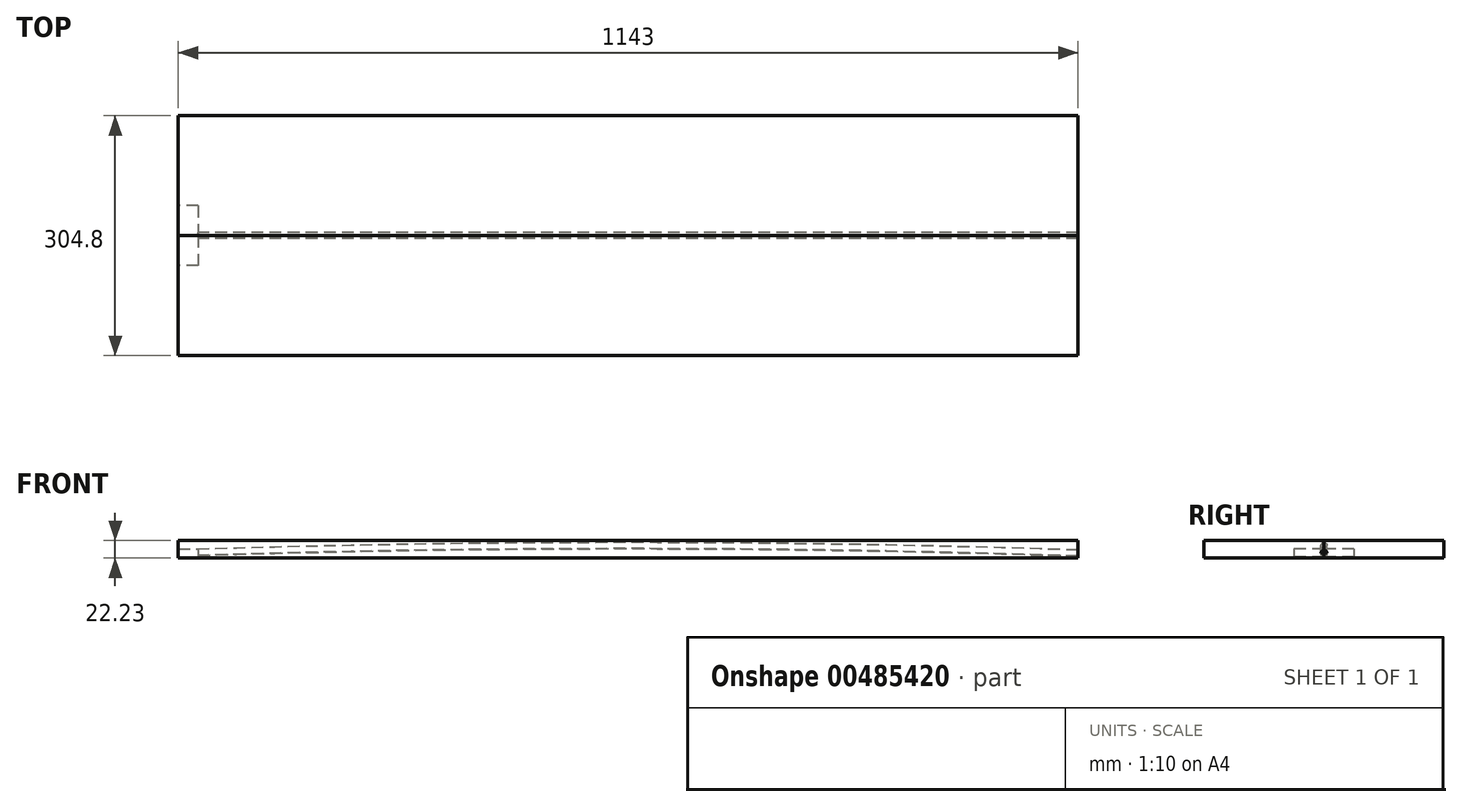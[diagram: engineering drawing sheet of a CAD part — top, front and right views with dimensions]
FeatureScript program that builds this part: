
annotation { "Feature Type Name" : "Feature", "Feature Type Description" : "" }
export const myFeature = defineFeature(function(context is Context, id is Id, definition is map)
    precondition{}
    {
        {
            var Q0;
            Q0=qCreatedBy(makeId("Front.planeOp"),FACE);
            var sketch = newSketch(context, id + "F0", { "sketchPlane" : qUnion([Q0])});
            skLineSegment(sketch, "E0.bottom", {"start": v(0, -22.23) * mm, "end": v(-1143, -22.23) * mm});
            skLineSegment(sketch, "E0.top", {"start": v(0, 0) * mm, "end": v(-1143, 0) * mm});
            skLineSegment(sketch, "E0.left", {"start": v(0, -22.23) * mm, "end": v(0, 0) * mm});
            skLineSegment(sketch, "E0.right", {"start": v(-1143, -22.23) * mm, "end": v(-1143, 0) * mm});
            skSolve(sketch);
        }
        {
            var Q0;
            Q0=makeQuery(id+"F0.imprint","IMPRINT",FACE,{"disambiguationData":[TD([[makeQuery(id+"F0.imprint","IMPRINT",EDGE,{"derivedFrom":sQuery(id+"F0.wireOp",EDGE,"E0.bottom")}),-1.0]])]});
            extrude(context, id + "F1", {"entities" : qUnion([Q0]), "oppositeDirection" : true, "depth" : 152.4 * mm});
        }
        {
            var Q0;
            Q0=makeQuery(id+"F1.opExtrude","CAP_FACE",FACE,{"disambiguationData":[OSD([sQuery(id+"F0.wireOp",EDGE,"E0.bottom"),sQuery(id+"F0.wireOp",EDGE,"E0.top"),sQuery(id+"F0.wireOp",EDGE,"E0.left"),sQuery(id+"F0.wireOp",EDGE,"E0.right")])],"isStart":true});
            extrude(context, id + "F2", {"entities" : qUnion([Q0]), "depth" : 152.4 * mm});
        }
        {
            var Q0;
            Q0=makeQuery(id+"F1.opExtrude","CAP_FACE",FACE,{"disambiguationData":[OSD([sQuery(id+"F0.wireOp",EDGE,"E0.bottom"),sQuery(id+"F0.wireOp",EDGE,"E0.top"),sQuery(id+"F0.wireOp",EDGE,"E0.left"),sQuery(id+"F0.wireOp",EDGE,"E0.right")])],"isStart":true});
            var sketch = newSketch(context, id + "F3", { "sketchPlane" : qUnion([Q0])});
            skArc(sketch, "E1", {"start": v(0, -15.87) * mm, "mid": v(-571.5, -6.35) * mm, "end": v(-1143, -15.87) * mm});
            skSolve(sketch);
        }
        {
            var Q0;
            Q0=makeQuery(id+"F1.opExtrude","SWEPT_FACE",FACE,{"disambiguationData":[OSD([sQuery(id+"F0.wireOp",EDGE,"E0.right")])]});
            var sketch = newSketch(context, id + "F4", { "sketchPlane" : qUnion([Q0])});
            skCircle(sketch, "E2", {"center": v(0, -15.87) * mm, "radius": 3.81 * mm});
            skLineSegment(sketch, "E3.bottom", {"start": v(-38.1, -10.5) * mm, "end": v(38.1, -10.5) * mm});
            skLineSegment(sketch, "E3.top", {"start": v(-38.1, -20.67) * mm, "end": v(38.1, -20.67) * mm});
            skLineSegment(sketch, "E3.left", {"start": v(-38.1, -10.5) * mm, "end": v(-38.1, -20.67) * mm});
            skLineSegment(sketch, "E3.right", {"start": v(38.1, -10.5) * mm, "end": v(38.1, -20.67) * mm});
            skSolve(sketch);
        }
        {
            var Q0;
            {var subQ0=sQuery(id+"F4.wireOp",EDGE,"E2");var subQ1=makeQuery(id+"F1.opExtrude","CAP_EDGE",EDGE,{"disambiguationData":[OSD([sQuery(id+"F0.wireOp",EDGE,"E0.right")])],"isStart":true});var subQ2=makeQuery(id+"F4.imprint","INTERSECT",VERTEX,{"disambiguationData":[OD(0.0)],"derivedFrom":[subQ1,subQ0]});Q0=makeQuery(id+"F4.imprint","IMPRINT",FACE,{"disambiguationData":[TD([[makeQuery(id+"F4.imprint","IMPRINT",EDGE,{"disambiguationData":[TD([[subQ2,-1.0]])],"derivedFrom":subQ0}),1.0]])]});}
            var Q1;
            {var subQ0=sQuery(id+"F4.wireOp",EDGE,"E2");var subQ1=makeQuery(id+"F1.opExtrude","CAP_EDGE",EDGE,{"disambiguationData":[OSD([sQuery(id+"F0.wireOp",EDGE,"E0.right")])],"isStart":true});var subQ2=makeQuery(id+"F4.imprint","INTERSECT",VERTEX,{"disambiguationData":[OD(0.0)],"derivedFrom":[subQ1,subQ0]});Q1=makeQuery(id+"F4.imprint","IMPRINT",FACE,{"disambiguationData":[TD([[makeQuery(id+"F4.imprint","IMPRINT",EDGE,{"disambiguationData":[TD([[subQ2,1.0]])],"derivedFrom":subQ0}),1.0]])]});}
            var Q2;
            Q2=sQuery(id+"F3.wireOp",EDGE,"E1");
            sweep(context, id + "F5", {"operationType" : NewBodyOperationType.REMOVE, "profiles" : qUnion([Q0, Q1]), "path" : qUnion([Q2])});
        }
        {
            var Q0;
            {var subQ0=sQuery(id+"F4.wireOp",EDGE,"E3.left");Q0=makeQuery(id+"F4.imprint","IMPRINT",FACE,{"disambiguationData":[TD([[makeQuery(id+"F4.imprint","IMPRINT",EDGE,{"derivedFrom":subQ0}),1.0]])]});}
            var Q1;
            {var subQ0=sQuery(id+"F4.wireOp",EDGE,"E3.right");Q1=makeQuery(id+"F4.imprint","IMPRINT",FACE,{"disambiguationData":[TD([[makeQuery(id+"F4.imprint","IMPRINT",EDGE,{"derivedFrom":subQ0}),-1.0]])]});}
            var Q2;
            {var subQ0=sQuery(id+"F4.wireOp",EDGE,"E2");var subQ1=makeQuery(id+"F1.opExtrude","CAP_EDGE",EDGE,{"disambiguationData":[OSD([sQuery(id+"F0.wireOp",EDGE,"E0.right")])],"isStart":true});var subQ2=makeQuery(id+"F4.imprint","INTERSECT",VERTEX,{"disambiguationData":[OD(0.0)],"derivedFrom":[subQ1,subQ0]});Q2=makeQuery(id+"F4.imprint","IMPRINT",FACE,{"disambiguationData":[TD([[makeQuery(id+"F4.imprint","IMPRINT",EDGE,{"disambiguationData":[TD([[subQ2,1.0]])],"derivedFrom":subQ0}),1.0]])]});}
            var Q3;
            {var subQ0=sQuery(id+"F4.wireOp",EDGE,"E2");var subQ1=makeQuery(id+"F1.opExtrude","CAP_EDGE",EDGE,{"disambiguationData":[OSD([sQuery(id+"F0.wireOp",EDGE,"E0.right")])],"isStart":true});var subQ2=makeQuery(id+"F4.imprint","INTERSECT",VERTEX,{"disambiguationData":[OD(0.0)],"derivedFrom":[subQ1,subQ0]});Q3=makeQuery(id+"F4.imprint","IMPRINT",FACE,{"disambiguationData":[TD([[makeQuery(id+"F4.imprint","IMPRINT",EDGE,{"disambiguationData":[TD([[subQ2,-1.0]])],"derivedFrom":subQ0}),1.0]])]});}
            extrude(context, id + "F6", {"entities" : qUnion([Q0, Q1, Q2, Q3]), "operationType" : NewBodyOperationType.REMOVE, "oppositeDirection" : true, "depth" : 25.4 * mm});
        }
    });
